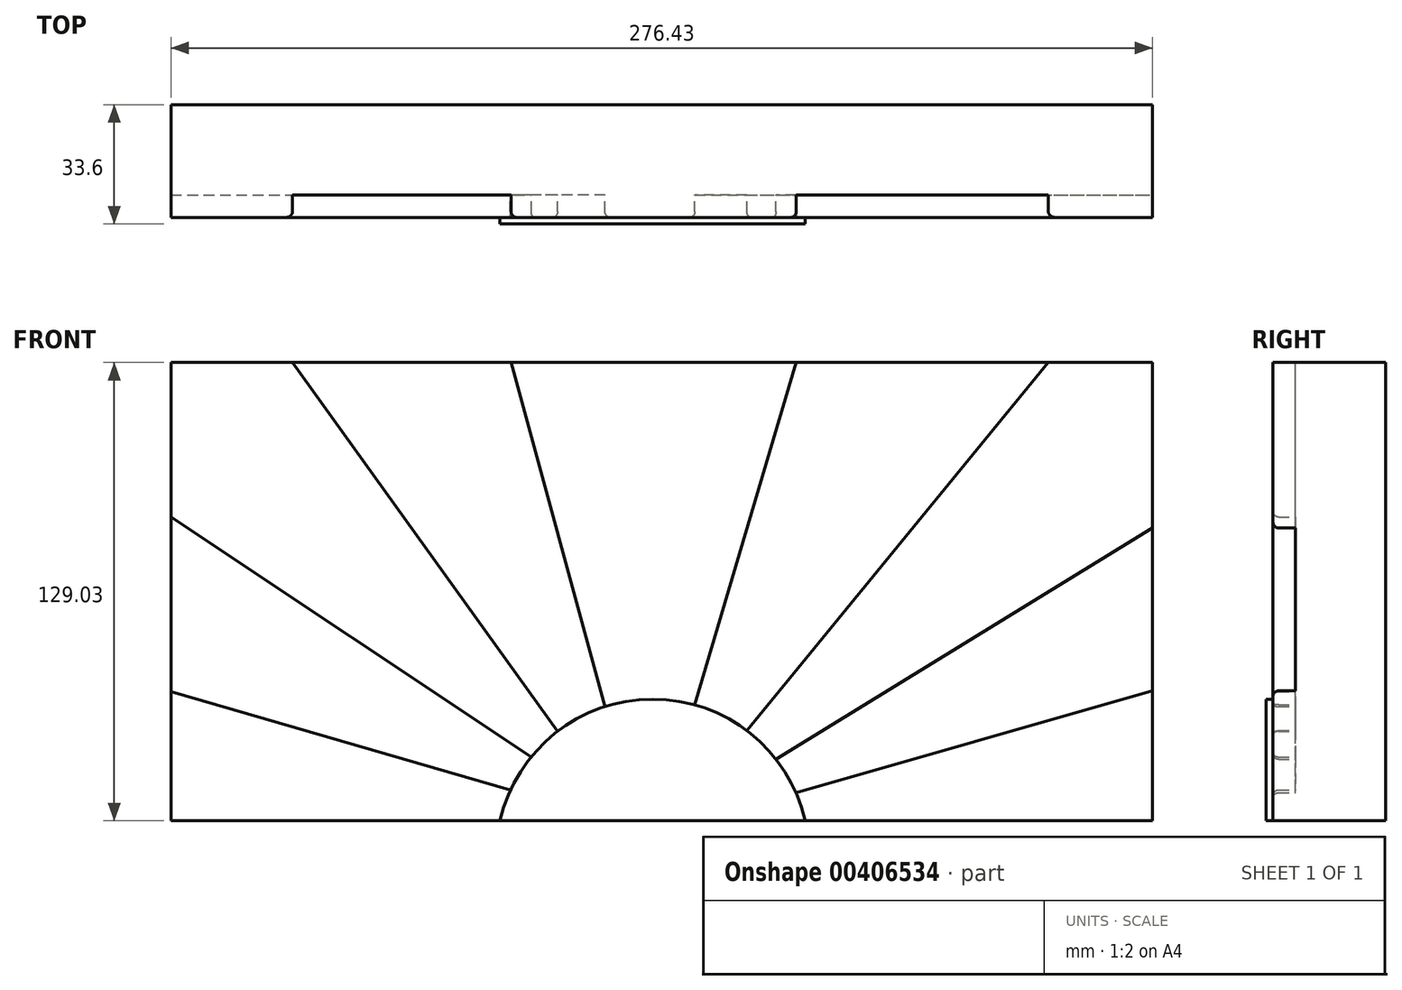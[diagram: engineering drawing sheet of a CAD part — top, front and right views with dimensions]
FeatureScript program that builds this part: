
annotation { "Feature Type Name" : "Feature", "Feature Type Description" : "" }
export const myFeature = defineFeature(function(context is Context, id is Id, definition is map)
    precondition{}
    {
        {
            var Q0;
            Q0=qCreatedBy(makeId("Front.planeOp"),FACE);
            var sketch = newSketch(context, id + "F0", { "sketchPlane" : qUnion([Q0])});
            skLineSegment(sketch, "E0.bottom", {"start": v(-135.86, 0) * mm, "end": v(140.57, 0) * mm});
            skLineSegment(sketch, "E0.top", {"start": v(-135.86, 129.03) * mm, "end": v(140.57, 129.03) * mm});
            skLineSegment(sketch, "E0.left", {"start": v(-135.86, 0) * mm, "end": v(-135.86, 129.03) * mm});
            skLineSegment(sketch, "E0.right", {"start": v(140.57, 0) * mm, "end": v(140.57, 129.03) * mm});
            skSolve(sketch);
        }
        {
            var Q0;
            Q0=makeQuery(id+"F0.imprint","IMPRINT",FACE,{"disambiguationData":[TD([[makeQuery(id+"F0.imprint","IMPRINT",EDGE,{"derivedFrom":sQuery(id+"F0.wireOp",EDGE,"E0.bottom")}),1.0]])]});
            extrude(context, id + "F1", {"entities" : qUnion([Q0]), "depth" : 25.4 * mm});
        }
        {
            var Q0;
            Q0=makeQuery(id+"F1.opExtrude","CAP_FACE",FACE,{"disambiguationData":[OSD([sQuery(id+"F0.wireOp",EDGE,"E0.bottom"),sQuery(id+"F0.wireOp",EDGE,"E0.top"),sQuery(id+"F0.wireOp",EDGE,"E0.left"),sQuery(id+"F0.wireOp",EDGE,"E0.right")])],"isStart":false});
            var sketch = newSketch(context, id + "F2", { "sketchPlane" : qUnion([Q0])});
            skArc(sketch, "E1", {"start": v(42.75, 0) * mm, "mid": v(-0.23, 34.27) * mm, "end": v(-43.22, 0) * mm});
            skSolve(sketch);
        }
        {
            var Q0;
            {var subQ0=sQuery(id+"F2.wireOp",EDGE,"E1");Q0=makeQuery(id+"F2.imprint","IMPRINT",FACE,{"disambiguationData":[TD([[makeQuery(id+"F2.imprint","IMPRINT",EDGE,{"derivedFrom":subQ0}),1.0]])]});}
            extrude(context, id + "F3", {"entities" : qUnion([Q0]), "operationType" : NewBodyOperationType.ADD, "depth" : 8.2 * mm});
        }
        {
            var Q0;
            Q0=makeQuery(id+"F1.opExtrude","CAP_FACE",FACE,{"disambiguationData":[OSD([sQuery(id+"F0.wireOp",EDGE,"E0.bottom"),sQuery(id+"F0.wireOp",EDGE,"E0.top"),sQuery(id+"F0.wireOp",EDGE,"E0.left"),sQuery(id+"F0.wireOp",EDGE,"E0.right")])],"isStart":false});
            var sketch = newSketch(context, id + "F4", { "sketchPlane" : qUnion([Q0])});
            skLineSegment(sketch, "E2", {"start": v(40.14, 7.9) * mm, "end": v(140.57, 36.6) * mm});
            skLineSegment(sketch, "E3", {"start": v(34.5, 17.33) * mm, "end": v(140.57, 82.44) * mm});
            skLineSegment(sketch, "E4", {"start": v(26.29, 25.4) * mm, "end": v(111.2, 129.03) * mm});
            skLineSegment(sketch, "E5", {"start": v(11.64, 32.64) * mm, "end": v(40.19, 129.03) * mm});
            skLineSegment(sketch, "E6", {"start": v(-13.65, 32.17) * mm, "end": v(-40.08, 129.03) * mm});
            skLineSegment(sketch, "E7", {"start": v(-27.04, 25.18) * mm, "end": v(-101.66, 129.03) * mm});
            skLineSegment(sketch, "E8", {"start": v(-135.86, 85.52) * mm, "end": v(-34.43, 18) * mm});
            skLineSegment(sketch, "E9", {"start": v(-40.28, 8.62) * mm, "end": v(-135.86, 36.37) * mm});
            skSolve(sketch);
        }
        {
            var Q0;
            {var subQ0=sQuery(id+"F4.wireOp",EDGE,"E9");Q0=makeQuery(id+"F4.imprint","IMPRINT",FACE,{"disambiguationData":[TD([[makeQuery(id+"F4.imprint","IMPRINT",EDGE,{"derivedFrom":subQ0}),1.0]])]});}
            var Q1;
            {var subQ4=sQuery(id+"F4.wireOp",EDGE,"E7");Q1=makeQuery(id+"F4.imprint","IMPRINT",FACE,{"disambiguationData":[TD([[makeQuery(id+"F4.imprint","IMPRINT",EDGE,{"derivedFrom":subQ4}),1.0]])]});}
            var Q2;
            {var subQ0=sQuery(id+"F4.wireOp",EDGE,"E5");Q2=makeQuery(id+"F4.imprint","IMPRINT",FACE,{"disambiguationData":[TD([[makeQuery(id+"F4.imprint","IMPRINT",EDGE,{"derivedFrom":subQ0}),1.0]])]});}
            var Q3;
            {var subQ3=sQuery(id+"F4.wireOp",EDGE,"E3");Q3=makeQuery(id+"F4.imprint","IMPRINT",FACE,{"disambiguationData":[TD([[makeQuery(id+"F4.imprint","IMPRINT",EDGE,{"derivedFrom":subQ3}),1.0]])]});}
            var Q4;
            {var subQ0=sQuery(id+"F4.wireOp",EDGE,"E2");Q4=makeQuery(id+"F4.imprint","IMPRINT",FACE,{"disambiguationData":[TD([[makeQuery(id+"F4.imprint","IMPRINT",EDGE,{"derivedFrom":subQ0}),-1.0]])]});}
            extrude(context, id + "F5", {"entities" : qUnion([Q0, Q1, Q2, Q3, Q4]), "operationType" : NewBodyOperationType.ADD, "depth" : 6.35 * mm});
        }
        {
            var Q0;
            Q0=makeQuery(id+"F5.opExtrude","CAP_EDGE",EDGE,{"disambiguationData":[OSD([sQuery(id+"F4.wireOp",EDGE,"E2")])],"isStart":false});
            var Q1;
            Q1=makeQuery(id+"F5.opExtrude","CAP_EDGE",EDGE,{"disambiguationData":[OSD([sQuery(id+"F4.wireOp",EDGE,"E3")])],"isStart":false});
            var Q2;
            Q2=makeQuery(id+"F5.opExtrude","CAP_EDGE",EDGE,{"disambiguationData":[OSD([sQuery(id+"F4.wireOp",EDGE,"E4")])],"isStart":false});
            var Q3;
            Q3=makeQuery(id+"F5.opExtrude","CAP_EDGE",EDGE,{"disambiguationData":[OSD([sQuery(id+"F4.wireOp",EDGE,"E5")])],"isStart":false});
            var Q4;
            Q4=makeQuery(id+"F5.opExtrude","CAP_EDGE",EDGE,{"disambiguationData":[OSD([sQuery(id+"F4.wireOp",EDGE,"E6")])],"isStart":false});
            var Q5;
            Q5=makeQuery(id+"F5.opExtrude","CAP_EDGE",EDGE,{"disambiguationData":[OSD([sQuery(id+"F4.wireOp",EDGE,"E7")])],"isStart":false});
            var Q6;
            Q6=makeQuery(id+"F5.opExtrude","CAP_EDGE",EDGE,{"disambiguationData":[OSD([sQuery(id+"F4.wireOp",EDGE,"E8")])],"isStart":false});
            var Q7;
            Q7=makeQuery(id+"F5.opExtrude","CAP_EDGE",EDGE,{"disambiguationData":[OSD([sQuery(id+"F4.wireOp",EDGE,"E9")])],"isStart":false});
            fillet(context, id + "F6", {"entities" : qUnion([Q0, Q1, Q2, Q3, Q4, Q5, Q6, Q7]), "radius" : 1.59 * mm, "tangentPropagation" : true, "allowEdgeOverflow" : false});
        }
    });
